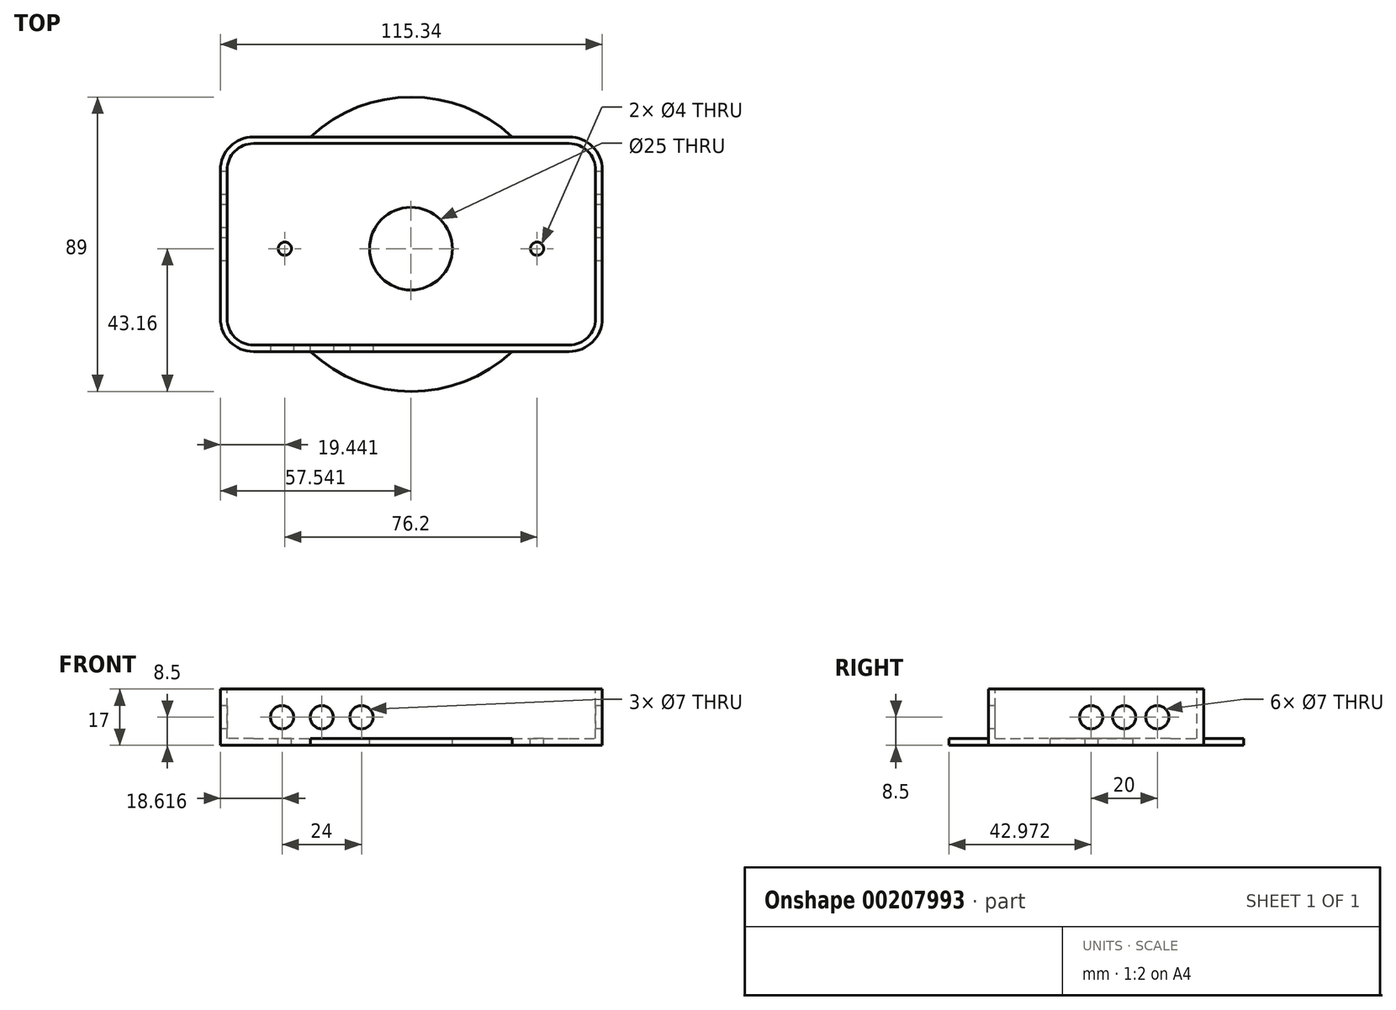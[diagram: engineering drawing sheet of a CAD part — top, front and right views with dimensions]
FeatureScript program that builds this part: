
annotation { "Feature Type Name" : "Feature", "Feature Type Description" : "" }
export const myFeature = defineFeature(function(context is Context, id is Id, definition is map)
    precondition{}
    {
        {
            var Q0;
            Q0=qCreatedBy(makeId("Top.planeOp"),FACE);
            var sketch = newSketch(context, id + "F0", { "sketchPlane" : qUnion([Q0])});
            skCircle(sketch, "E0", {"center": v(-41.46, 25.61) * mm, "radius": 3.2 * mm});
            skCircle(sketch, "E1", {"center": v(52.64, 25.61) * mm, "radius": 3.2 * mm});
            skCircle(sketch, "E2", {"center": v(52.64, -22.93) * mm, "radius": 3.2 * mm});
            skCircle(sketch, "E3", {"center": v(-41.46, -22.93) * mm, "radius": 3.2 * mm});
            skLineSegment(sketch, "E4.bottom", {"start": v(-44.66, 28.81) * mm, "end": v(55.84, 28.81) * mm});
            skLineSegment(sketch, "E4.top", {"start": v(-44.66, -26.13) * mm, "end": v(55.84, -26.13) * mm});
            skLineSegment(sketch, "E4.left", {"start": v(-44.66, 28.81) * mm, "end": v(-44.66, -26.13) * mm});
            skLineSegment(sketch, "E4.right", {"start": v(55.84, 28.81) * mm, "end": v(55.84, -26.13) * mm});
            skLineSegment(sketch, "E5.bottom", {"start": v(-29.74, 26.84) * mm, "end": v(45.76, 26.84) * mm});
            skLineSegment(sketch, "E5.top", {"start": v(-29.74, -24.16) * mm, "end": v(45.76, -24.16) * mm});
            skLineSegment(sketch, "E5.left", {"start": v(-29.74, 26.84) * mm, "end": v(-29.74, -24.16) * mm});
            skLineSegment(sketch, "E5.right", {"start": v(45.76, 26.84) * mm, "end": v(45.76, -24.16) * mm});
            skLineSegment(sketch, "E6.bottom", {"start": v(-39.66, 33.81) * mm, "end": v(55.68, 33.81) * mm});
            skLineSegment(sketch, "E6.top", {"start": v(-39.66, -31.13) * mm, "end": v(55.68, -31.13) * mm});
            skLineSegment(sketch, "E6.left", {"start": v(-49.66, 23.81) * mm, "end": v(-49.66, -21.13) * mm});
            skLineSegment(sketch, "E6.right", {"start": v(65.68, 23.81) * mm, "end": v(65.68, -21.13) * mm});
            skCircle(sketch, "E7", {"center": v(8, 1.34) * mm, "radius": 44.5 * mm});
            skPoint(sketch, "E7.centerSnap0", {"position": v(8, -24.16) * mm});
            skPoint(sketch, "E7.centerSnap1", {"position": v(-29.74, 1.34) * mm});
            skPoint(sketch, "E8.visualSharp", {"position": v(65.68, 33.81) * mm});
            skArc(sketch, "E8.filletArc", {"start": v(65.68, 23.81) * mm, "mid": v(62.75, 30.88) * mm, "end": v(55.68, 33.81) * mm});
            skPoint(sketch, "E9.visualSharp", {"position": v(-49.66, 33.81) * mm});
            skArc(sketch, "E9.filletArc", {"start": v(-39.66, 33.81) * mm, "mid": v(-46.74, 30.88) * mm, "end": v(-49.66, 23.81) * mm});
            skPoint(sketch, "E10.visualSharp", {"position": v(-49.66, -31.13) * mm});
            skArc(sketch, "E10.filletArc", {"start": v(-49.66, -21.13) * mm, "mid": v(-46.74, -28.2) * mm, "end": v(-39.66, -31.13) * mm});
            skPoint(sketch, "E11.visualSharp", {"position": v(65.68, -31.13) * mm});
            skArc(sketch, "E11.filletArc", {"start": v(55.68, -31.13) * mm, "mid": v(62.75, -28.2) * mm, "end": v(65.68, -21.13) * mm});
            skSolve(sketch);
        }
        {
            var Q0;
            {var subQ1=sQuery(id+"F0.wireOp",EDGE,"E4.bottom");var subQ13=sQuery(id+"F0.wireOp",EDGE,"E0");var subQ20=makeQuery(id+"F0.imprint","INTERSECT",VERTEX,{"disambiguationData":[OD(1.0)],"derivedFrom":[subQ13,subQ1]});Q0=makeQuery(id+"F0.imprint","IMPRINT",FACE,{"disambiguationData":[TD([[makeQuery(id+"F0.imprint","IMPRINT",EDGE,{"disambiguationData":[TD([[subQ20,1.0]])],"derivedFrom":subQ13}),-1.0]])]});}
            var Q1;
            {var subQ0=sQuery(id+"F0.wireOp",EDGE,"E7");var subQ7=sQuery(id+"F0.wireOp",EDGE,"E5.bottom");var subQ12=makeQuery(id+"F0.imprint","INTERSECT",VERTEX,{"disambiguationData":[OD(0.0)],"derivedFrom":[subQ7,subQ0]});Q1=makeQuery(id+"F0.imprint","IMPRINT",FACE,{"disambiguationData":[TD([[makeQuery(id+"F0.imprint","IMPRINT",EDGE,{"disambiguationData":[TD([[subQ12,-1.0]])],"derivedFrom":subQ7}),-1.0]])]});}
            var Q2;
            {var subQ0=sQuery(id+"F0.wireOp",EDGE,"E4.bottom");var subQ1=sQuery(id+"F0.wireOp",EDGE,"E1");var subQ2=makeQuery(id+"F0.imprint","INTERSECT",VERTEX,{"disambiguationData":[OD(0.0)],"derivedFrom":[subQ1,subQ0]});Q2=makeQuery(id+"F0.imprint","IMPRINT",FACE,{"disambiguationData":[TD([[makeQuery(id+"F0.imprint","IMPRINT",EDGE,{"disambiguationData":[TD([[subQ2,1.0]])],"derivedFrom":subQ1}),1.0]])]});}
            var Q3;
            {var subQ0=sQuery(id+"F0.wireOp",EDGE,"E4.left");var subQ1=sQuery(id+"F0.wireOp",EDGE,"E3");var subQ2=makeQuery(id+"F0.imprint","INTERSECT",VERTEX,{"disambiguationData":[OD(0.0)],"derivedFrom":[subQ1,subQ0]});Q3=makeQuery(id+"F0.imprint","IMPRINT",FACE,{"disambiguationData":[TD([[makeQuery(id+"F0.imprint","IMPRINT",EDGE,{"disambiguationData":[TD([[subQ2,-1.0]])],"derivedFrom":subQ1}),1.0]])]});}
            var Q4;
            {var subQ0=sQuery(id+"F0.wireOp",EDGE,"E7");var subQ1=sQuery(id+"F0.wireOp",EDGE,"E4.top");var subQ2=makeQuery(id+"F0.imprint","INTERSECT",VERTEX,{"disambiguationData":[OD(0.0)],"derivedFrom":[subQ1,subQ0]});Q4=makeQuery(id+"F0.imprint","IMPRINT",FACE,{"disambiguationData":[TD([[makeQuery(id+"F0.imprint","IMPRINT",EDGE,{"disambiguationData":[TD([[subQ2,-1.0]])],"derivedFrom":subQ1}),-1.0]])]});}
            var Q5;
            {var subQ0=sQuery(id+"F0.wireOp",EDGE,"E7");var subQ1=sQuery(id+"F0.wireOp",EDGE,"E4.top");var subQ2=makeQuery(id+"F0.imprint","INTERSECT",VERTEX,{"disambiguationData":[OD(0.0)],"derivedFrom":[subQ1,subQ0]});Q5=makeQuery(id+"F0.imprint","IMPRINT",FACE,{"disambiguationData":[TD([[makeQuery(id+"F0.imprint","IMPRINT",EDGE,{"disambiguationData":[TD([[subQ2,-1.0]])],"derivedFrom":subQ1}),1.0]])]});}
            var Q6;
            {var subQ0=sQuery(id+"F0.wireOp",EDGE,"E7");var subQ1=sQuery(id+"F0.wireOp",EDGE,"E6.top");var subQ2=makeQuery(id+"F0.imprint","INTERSECT",VERTEX,{"disambiguationData":[OD(0.0)],"derivedFrom":[subQ1,subQ0]});Q6=makeQuery(id+"F0.imprint","IMPRINT",FACE,{"disambiguationData":[TD([[makeQuery(id+"F0.imprint","IMPRINT",EDGE,{"disambiguationData":[TD([[subQ2,-1.0]])],"derivedFrom":subQ1}),-1.0]])]});}
            var Q7;
            {var subQ0=sQuery(id+"F0.wireOp",EDGE,"E7");var subQ1=sQuery(id+"F0.wireOp",EDGE,"E6.bottom");var subQ2=makeQuery(id+"F0.imprint","INTERSECT",VERTEX,{"disambiguationData":[OD(0.0)],"derivedFrom":[subQ1,subQ0]});Q7=makeQuery(id+"F0.imprint","IMPRINT",FACE,{"disambiguationData":[TD([[makeQuery(id+"F0.imprint","IMPRINT",EDGE,{"disambiguationData":[TD([[subQ2,-1.0]])],"derivedFrom":subQ1}),1.0]])]});}
            var Q8;
            Q8=makeQuery(id+"F0.imprint","IMPRINT",FACE,{"disambiguationData":[TD([[makeQuery(id+"F0.imprint","IMPRINT",EDGE,{"derivedFrom":sQuery(id+"F0.wireOp",EDGE,"E6.right")}),-1.0]])]});
            var Q9;
            {var subQ1=sQuery(id+"F0.wireOp",EDGE,"E4.bottom");var subQ5=sQuery(id+"F0.wireOp",EDGE,"E1");var subQ6=makeQuery(id+"F0.imprint","INTERSECT",VERTEX,{"disambiguationData":[OD(1.0)],"derivedFrom":[subQ5,subQ1]});Q9=makeQuery(id+"F0.imprint","IMPRINT",FACE,{"disambiguationData":[TD([[makeQuery(id+"F0.imprint","IMPRINT",EDGE,{"disambiguationData":[TD([[subQ6,-1.0]])],"derivedFrom":subQ5}),-1.0]])]});}
            var Q10;
            {var subQ0=sQuery(id+"F0.wireOp",EDGE,"E4.bottom");var subQ1=sQuery(id+"F0.wireOp",EDGE,"E0");var subQ2=makeQuery(id+"F0.imprint","INTERSECT",VERTEX,{"disambiguationData":[OD(0.0)],"derivedFrom":[subQ1,subQ0]});Q10=makeQuery(id+"F0.imprint","IMPRINT",FACE,{"disambiguationData":[TD([[makeQuery(id+"F0.imprint","IMPRINT",EDGE,{"disambiguationData":[TD([[subQ2,-1.0]])],"derivedFrom":subQ1}),1.0]])]});}
            var Q11;
            {var subQ0=sQuery(id+"F0.wireOp",EDGE,"E7");var subQ1=sQuery(id+"F0.wireOp",EDGE,"E4.bottom");var subQ2=makeQuery(id+"F0.imprint","INTERSECT",VERTEX,{"disambiguationData":[OD(0.0)],"derivedFrom":[subQ1,subQ0]});Q11=makeQuery(id+"F0.imprint","IMPRINT",FACE,{"disambiguationData":[TD([[makeQuery(id+"F0.imprint","IMPRINT",EDGE,{"disambiguationData":[TD([[subQ2,-1.0]])],"derivedFrom":subQ1}),-1.0]])]});}
            var Q12;
            {var subQ0=sQuery(id+"F0.wireOp",EDGE,"E7");var subQ1=sQuery(id+"F0.wireOp",EDGE,"E5.left");var subQ2=makeQuery(id+"F0.imprint","INTERSECT",VERTEX,{"disambiguationData":[OD(0.0)],"derivedFrom":[subQ1,subQ0]});Q12=makeQuery(id+"F0.imprint","IMPRINT",FACE,{"disambiguationData":[TD([[makeQuery(id+"F0.imprint","IMPRINT",EDGE,{"disambiguationData":[TD([[subQ2,-1.0]])],"derivedFrom":subQ1}),-1.0]])]});}
            var Q13;
            Q13=makeQuery(id+"F0.imprint","IMPRINT",FACE,{"disambiguationData":[TD([[makeQuery(id+"F0.imprint","IMPRINT",EDGE,{"derivedFrom":sQuery(id+"F0.wireOp",EDGE,"E6.left")}),1.0]])]});
            var Q14;
            {var subQ0=sQuery(id+"F0.wireOp",EDGE,"E4.top");var subQ1=sQuery(id+"F0.wireOp",EDGE,"E2");var subQ2=makeQuery(id+"F0.imprint","INTERSECT",VERTEX,{"disambiguationData":[OD(0.0)],"derivedFrom":[subQ1,subQ0]});Q14=makeQuery(id+"F0.imprint","IMPRINT",FACE,{"disambiguationData":[TD([[makeQuery(id+"F0.imprint","IMPRINT",EDGE,{"disambiguationData":[TD([[subQ2,1.0]])],"derivedFrom":subQ1}),1.0]])]});}
            var Q15;
            {var subQ0=sQuery(id+"F0.wireOp",EDGE,"E7");var subQ1=sQuery(id+"F0.wireOp",EDGE,"E5.right");var subQ2=makeQuery(id+"F0.imprint","INTERSECT",VERTEX,{"disambiguationData":[OD(0.0)],"derivedFrom":[subQ1,subQ0]});Q15=makeQuery(id+"F0.imprint","IMPRINT",FACE,{"disambiguationData":[TD([[makeQuery(id+"F0.imprint","IMPRINT",EDGE,{"disambiguationData":[TD([[subQ2,-1.0]])],"derivedFrom":subQ1}),1.0]])]});}
            var Q16;
            {var subQ0=sQuery(id+"F0.wireOp",EDGE,"E7");var subQ1=sQuery(id+"F0.wireOp",EDGE,"E4.bottom");var subQ2=makeQuery(id+"F0.imprint","INTERSECT",VERTEX,{"disambiguationData":[OD(0.0)],"derivedFrom":[subQ1,subQ0]});Q16=makeQuery(id+"F0.imprint","IMPRINT",FACE,{"disambiguationData":[TD([[makeQuery(id+"F0.imprint","IMPRINT",EDGE,{"disambiguationData":[TD([[subQ2,-1.0]])],"derivedFrom":subQ1}),1.0]])]});}
            var Q17;
            {var subQ0=sQuery(id+"F0.wireOp",EDGE,"E5.right");var subQ1=sQuery(id+"F0.wireOp",EDGE,"E5.top");var subQ2=makeQuery(id+"F0.imprint","INTERSECT",VERTEX,{"derivedFrom":[subQ1,subQ0]});Q17=makeQuery(id+"F0.imprint","IMPRINT",FACE,{"disambiguationData":[TD([[makeQuery(id+"F0.imprint","IMPRINT",EDGE,{"disambiguationData":[TD([[subQ2,1.0]])],"derivedFrom":subQ1}),1.0]])]});}
            var Q18;
            {var subQ0=sQuery(id+"F0.wireOp",EDGE,"E4.left");var subQ1=sQuery(id+"F0.wireOp",EDGE,"E3");var subQ2=makeQuery(id+"F0.imprint","INTERSECT",VERTEX,{"disambiguationData":[OD(0.0)],"derivedFrom":[subQ1,subQ0]});Q18=makeQuery(id+"F0.imprint","IMPRINT",FACE,{"disambiguationData":[TD([[makeQuery(id+"F0.imprint","IMPRINT",EDGE,{"disambiguationData":[TD([[subQ2,1.0]])],"derivedFrom":subQ1}),1.0]])]});}
            var Q19;
            {var subQ0=sQuery(id+"F0.wireOp",EDGE,"E4.left");var subQ1=sQuery(id+"F0.wireOp",EDGE,"E3");var subQ2=makeQuery(id+"F0.imprint","INTERSECT",VERTEX,{"disambiguationData":[OD(0.0)],"derivedFrom":[subQ1,subQ0]});Q19=makeQuery(id+"F0.imprint","IMPRINT",FACE,{"disambiguationData":[TD([[makeQuery(id+"F0.imprint","IMPRINT",EDGE,{"disambiguationData":[TD([[subQ2,-1.0]])],"derivedFrom":subQ1}),-1.0]])]});}
            var Q20;
            {var subQ0=sQuery(id+"F0.wireOp",EDGE,"E4.right");var subQ1=sQuery(id+"F0.wireOp",EDGE,"E2");var subQ2=makeQuery(id+"F0.imprint","INTERSECT",VERTEX,{"disambiguationData":[OD(0.0)],"derivedFrom":[subQ1,subQ0]});Q20=makeQuery(id+"F0.imprint","IMPRINT",FACE,{"disambiguationData":[TD([[makeQuery(id+"F0.imprint","IMPRINT",EDGE,{"disambiguationData":[TD([[subQ2,1.0]])],"derivedFrom":subQ1}),1.0]])]});}
            var Q21;
            {var subQ0=sQuery(id+"F0.wireOp",EDGE,"E4.top");var subQ1=sQuery(id+"F0.wireOp",EDGE,"E2");var subQ2=makeQuery(id+"F0.imprint","INTERSECT",VERTEX,{"disambiguationData":[OD(1.0)],"derivedFrom":[subQ1,subQ0]});Q21=makeQuery(id+"F0.imprint","IMPRINT",FACE,{"disambiguationData":[TD([[makeQuery(id+"F0.imprint","IMPRINT",EDGE,{"disambiguationData":[TD([[subQ2,-1.0]])],"derivedFrom":subQ1}),-1.0]])]});}
            var Q22;
            {var subQ0=sQuery(id+"F0.wireOp",EDGE,"E4.top");var subQ1=sQuery(id+"F0.wireOp",EDGE,"E2");var subQ2=makeQuery(id+"F0.imprint","INTERSECT",VERTEX,{"disambiguationData":[OD(0.0)],"derivedFrom":[subQ1,subQ0]});Q22=makeQuery(id+"F0.imprint","IMPRINT",FACE,{"disambiguationData":[TD([[makeQuery(id+"F0.imprint","IMPRINT",EDGE,{"disambiguationData":[TD([[subQ2,-1.0]])],"derivedFrom":subQ1}),1.0]])]});}
            var Q23;
            {var subQ0=sQuery(id+"F0.wireOp",EDGE,"E4.bottom");var subQ1=sQuery(id+"F0.wireOp",EDGE,"E1");var subQ2=makeQuery(id+"F0.imprint","INTERSECT",VERTEX,{"disambiguationData":[OD(0.0)],"derivedFrom":[subQ1,subQ0]});Q23=makeQuery(id+"F0.imprint","IMPRINT",FACE,{"disambiguationData":[TD([[makeQuery(id+"F0.imprint","IMPRINT",EDGE,{"disambiguationData":[TD([[subQ2,-1.0]])],"derivedFrom":subQ1}),1.0]])]});}
            var Q24;
            {var subQ0=sQuery(id+"F0.wireOp",EDGE,"E4.right");var subQ1=sQuery(id+"F0.wireOp",EDGE,"E1");var subQ2=makeQuery(id+"F0.imprint","INTERSECT",VERTEX,{"disambiguationData":[OD(0.0)],"derivedFrom":[subQ1,subQ0]});Q24=makeQuery(id+"F0.imprint","IMPRINT",FACE,{"disambiguationData":[TD([[makeQuery(id+"F0.imprint","IMPRINT",EDGE,{"disambiguationData":[TD([[subQ2,1.0]])],"derivedFrom":subQ1}),1.0]])]});}
            var Q25;
            {var subQ0=sQuery(id+"F0.wireOp",EDGE,"E4.bottom");var subQ1=sQuery(id+"F0.wireOp",EDGE,"E1");var subQ2=makeQuery(id+"F0.imprint","INTERSECT",VERTEX,{"disambiguationData":[OD(0.0)],"derivedFrom":[subQ1,subQ0]});Q25=makeQuery(id+"F0.imprint","IMPRINT",FACE,{"disambiguationData":[TD([[makeQuery(id+"F0.imprint","IMPRINT",EDGE,{"disambiguationData":[TD([[subQ2,1.0]])],"derivedFrom":subQ1}),-1.0]])]});}
            var Q26;
            {var subQ0=sQuery(id+"F0.wireOp",EDGE,"E4.left");var subQ1=sQuery(id+"F0.wireOp",EDGE,"E0");var subQ2=makeQuery(id+"F0.imprint","INTERSECT",VERTEX,{"disambiguationData":[OD(0.0)],"derivedFrom":[subQ1,subQ0]});Q26=makeQuery(id+"F0.imprint","IMPRINT",FACE,{"disambiguationData":[TD([[makeQuery(id+"F0.imprint","IMPRINT",EDGE,{"disambiguationData":[TD([[subQ2,-1.0]])],"derivedFrom":subQ1}),1.0]])]});}
            var Q27;
            {var subQ0=sQuery(id+"F0.wireOp",EDGE,"E4.bottom");var subQ1=sQuery(id+"F0.wireOp",EDGE,"E0");var subQ2=makeQuery(id+"F0.imprint","INTERSECT",VERTEX,{"disambiguationData":[OD(0.0)],"derivedFrom":[subQ1,subQ0]});Q27=makeQuery(id+"F0.imprint","IMPRINT",FACE,{"disambiguationData":[TD([[makeQuery(id+"F0.imprint","IMPRINT",EDGE,{"disambiguationData":[TD([[subQ2,-1.0]])],"derivedFrom":subQ1}),-1.0]])]});}
            var Q28;
            {var subQ0=sQuery(id+"F0.wireOp",EDGE,"E4.bottom");var subQ1=sQuery(id+"F0.wireOp",EDGE,"E0");var subQ2=makeQuery(id+"F0.imprint","INTERSECT",VERTEX,{"disambiguationData":[OD(0.0)],"derivedFrom":[subQ1,subQ0]});Q28=makeQuery(id+"F0.imprint","IMPRINT",FACE,{"disambiguationData":[TD([[makeQuery(id+"F0.imprint","IMPRINT",EDGE,{"disambiguationData":[TD([[subQ2,1.0]])],"derivedFrom":subQ1}),1.0]])]});}
            var Q29;
            {var subQ0=sQuery(id+"F0.wireOp",EDGE,"E5.left");var subQ1=sQuery(id+"F0.wireOp",EDGE,"E5.top");var subQ2=makeQuery(id+"F0.imprint","INTERSECT",VERTEX,{"derivedFrom":[subQ1,subQ0]});Q29=makeQuery(id+"F0.imprint","IMPRINT",FACE,{"disambiguationData":[TD([[makeQuery(id+"F0.imprint","IMPRINT",EDGE,{"disambiguationData":[TD([[subQ2,-1.0]])],"derivedFrom":subQ1}),1.0]])]});}
            var Q30;
            {var subQ0=sQuery(id+"F0.wireOp",EDGE,"E5.left");var subQ1=sQuery(id+"F0.wireOp",EDGE,"E5.bottom");var subQ2=makeQuery(id+"F0.imprint","INTERSECT",VERTEX,{"derivedFrom":[subQ1,subQ0]});Q30=makeQuery(id+"F0.imprint","IMPRINT",FACE,{"disambiguationData":[TD([[makeQuery(id+"F0.imprint","IMPRINT",EDGE,{"disambiguationData":[TD([[subQ2,-1.0]])],"derivedFrom":subQ1}),-1.0]])]});}
            var Q31;
            {var subQ0=sQuery(id+"F0.wireOp",EDGE,"E4.top");var subQ1=sQuery(id+"F0.wireOp",EDGE,"E3");var subQ2=makeQuery(id+"F0.imprint","INTERSECT",VERTEX,{"disambiguationData":[OD(0.0)],"derivedFrom":[subQ1,subQ0]});Q31=makeQuery(id+"F0.imprint","IMPRINT",FACE,{"disambiguationData":[TD([[makeQuery(id+"F0.imprint","IMPRINT",EDGE,{"disambiguationData":[TD([[subQ2,-1.0]])],"derivedFrom":subQ1}),1.0]])]});}
            var Q32;
            {var subQ0=sQuery(id+"F0.wireOp",EDGE,"E5.right");var subQ1=sQuery(id+"F0.wireOp",EDGE,"E5.bottom");var subQ2=makeQuery(id+"F0.imprint","INTERSECT",VERTEX,{"derivedFrom":[subQ1,subQ0]});Q32=makeQuery(id+"F0.imprint","IMPRINT",FACE,{"disambiguationData":[TD([[makeQuery(id+"F0.imprint","IMPRINT",EDGE,{"disambiguationData":[TD([[subQ2,1.0]])],"derivedFrom":subQ1}),-1.0]])]});}
            extrude(context, id + "F1", {"entities" : qUnion([Q0, Q1, Q2, Q3, Q4, Q5, Q6, Q7, Q8, Q9, Q10, Q11, Q12, Q13, Q14, Q15, Q16, Q17, Q18, Q19, Q20, Q21, Q22, Q23, Q24, Q25, Q26, Q27, Q28, Q29, Q30, Q31, Q32]), "oppositeDirection" : true, "depth" : 2 * mm});
        }
        {
            var Q0;
            Q0=makeQuery(id+"F0.imprint","IMPRINT",FACE,{"disambiguationData":[TD([[makeQuery(id+"F0.imprint","IMPRINT",EDGE,{"derivedFrom":sQuery(id+"F0.wireOp",EDGE,"E6.left")}),1.0]])]});
            var Q1;
            {var subQ0=sQuery(id+"F0.wireOp",EDGE,"E7");var subQ1=sQuery(id+"F0.wireOp",EDGE,"E4.bottom");var subQ2=makeQuery(id+"F0.imprint","INTERSECT",VERTEX,{"disambiguationData":[OD(0.0)],"derivedFrom":[subQ1,subQ0]});Q1=makeQuery(id+"F0.imprint","IMPRINT",FACE,{"disambiguationData":[TD([[makeQuery(id+"F0.imprint","IMPRINT",EDGE,{"disambiguationData":[TD([[subQ2,-1.0]])],"derivedFrom":subQ1}),1.0]])]});}
            var Q2;
            Q2=makeQuery(id+"F0.imprint","IMPRINT",FACE,{"disambiguationData":[TD([[makeQuery(id+"F0.imprint","IMPRINT",EDGE,{"derivedFrom":sQuery(id+"F0.wireOp",EDGE,"E6.right")}),-1.0]])]});
            var Q3;
            {var subQ1=sQuery(id+"F0.wireOp",EDGE,"E4.bottom");var subQ5=sQuery(id+"F0.wireOp",EDGE,"E1");var subQ6=makeQuery(id+"F0.imprint","INTERSECT",VERTEX,{"disambiguationData":[OD(1.0)],"derivedFrom":[subQ5,subQ1]});Q3=makeQuery(id+"F0.imprint","IMPRINT",FACE,{"disambiguationData":[TD([[makeQuery(id+"F0.imprint","IMPRINT",EDGE,{"disambiguationData":[TD([[subQ6,-1.0]])],"derivedFrom":subQ5}),-1.0]])]});}
            var Q4;
            {var subQ0=sQuery(id+"F0.wireOp",EDGE,"E4.bottom");var subQ1=sQuery(id+"F0.wireOp",EDGE,"E1");var subQ2=makeQuery(id+"F0.imprint","INTERSECT",VERTEX,{"disambiguationData":[OD(0.0)],"derivedFrom":[subQ1,subQ0]});Q4=makeQuery(id+"F0.imprint","IMPRINT",FACE,{"disambiguationData":[TD([[makeQuery(id+"F0.imprint","IMPRINT",EDGE,{"disambiguationData":[TD([[subQ2,1.0]])],"derivedFrom":subQ1}),1.0]])]});}
            var Q5;
            {var subQ0=sQuery(id+"F0.wireOp",EDGE,"E4.top");var subQ1=sQuery(id+"F0.wireOp",EDGE,"E2");var subQ2=makeQuery(id+"F0.imprint","INTERSECT",VERTEX,{"disambiguationData":[OD(0.0)],"derivedFrom":[subQ1,subQ0]});Q5=makeQuery(id+"F0.imprint","IMPRINT",FACE,{"disambiguationData":[TD([[makeQuery(id+"F0.imprint","IMPRINT",EDGE,{"disambiguationData":[TD([[subQ2,1.0]])],"derivedFrom":subQ1}),1.0]])]});}
            var Q6;
            {var subQ0=sQuery(id+"F0.wireOp",EDGE,"E7");var subQ1=sQuery(id+"F0.wireOp",EDGE,"E5.right");var subQ2=makeQuery(id+"F0.imprint","INTERSECT",VERTEX,{"disambiguationData":[OD(0.0)],"derivedFrom":[subQ1,subQ0]});Q6=makeQuery(id+"F0.imprint","IMPRINT",FACE,{"disambiguationData":[TD([[makeQuery(id+"F0.imprint","IMPRINT",EDGE,{"disambiguationData":[TD([[subQ2,-1.0]])],"derivedFrom":subQ1}),1.0]])]});}
            var Q7;
            {var subQ0=sQuery(id+"F0.wireOp",EDGE,"E7");var subQ7=sQuery(id+"F0.wireOp",EDGE,"E5.bottom");var subQ12=makeQuery(id+"F0.imprint","INTERSECT",VERTEX,{"disambiguationData":[OD(0.0)],"derivedFrom":[subQ7,subQ0]});Q7=makeQuery(id+"F0.imprint","IMPRINT",FACE,{"disambiguationData":[TD([[makeQuery(id+"F0.imprint","IMPRINT",EDGE,{"disambiguationData":[TD([[subQ12,-1.0]])],"derivedFrom":subQ7}),-1.0]])]});}
            var Q8;
            {var subQ0=sQuery(id+"F0.wireOp",EDGE,"E7");var subQ1=sQuery(id+"F0.wireOp",EDGE,"E4.bottom");var subQ2=makeQuery(id+"F0.imprint","INTERSECT",VERTEX,{"disambiguationData":[OD(0.0)],"derivedFrom":[subQ1,subQ0]});Q8=makeQuery(id+"F0.imprint","IMPRINT",FACE,{"disambiguationData":[TD([[makeQuery(id+"F0.imprint","IMPRINT",EDGE,{"disambiguationData":[TD([[subQ2,-1.0]])],"derivedFrom":subQ1}),-1.0]])]});}
            var Q9;
            {var subQ0=sQuery(id+"F0.wireOp",EDGE,"E7");var subQ1=sQuery(id+"F0.wireOp",EDGE,"E4.top");var subQ2=makeQuery(id+"F0.imprint","INTERSECT",VERTEX,{"disambiguationData":[OD(0.0)],"derivedFrom":[subQ1,subQ0]});Q9=makeQuery(id+"F0.imprint","IMPRINT",FACE,{"disambiguationData":[TD([[makeQuery(id+"F0.imprint","IMPRINT",EDGE,{"disambiguationData":[TD([[subQ2,-1.0]])],"derivedFrom":subQ1}),-1.0]])]});}
            var Q10;
            {var subQ0=sQuery(id+"F0.wireOp",EDGE,"E7");var subQ1=sQuery(id+"F0.wireOp",EDGE,"E4.top");var subQ2=makeQuery(id+"F0.imprint","INTERSECT",VERTEX,{"disambiguationData":[OD(0.0)],"derivedFrom":[subQ1,subQ0]});Q10=makeQuery(id+"F0.imprint","IMPRINT",FACE,{"disambiguationData":[TD([[makeQuery(id+"F0.imprint","IMPRINT",EDGE,{"disambiguationData":[TD([[subQ2,-1.0]])],"derivedFrom":subQ1}),1.0]])]});}
            var Q11;
            {var subQ0=sQuery(id+"F0.wireOp",EDGE,"E7");var subQ1=sQuery(id+"F0.wireOp",EDGE,"E5.left");var subQ2=makeQuery(id+"F0.imprint","INTERSECT",VERTEX,{"disambiguationData":[OD(0.0)],"derivedFrom":[subQ1,subQ0]});Q11=makeQuery(id+"F0.imprint","IMPRINT",FACE,{"disambiguationData":[TD([[makeQuery(id+"F0.imprint","IMPRINT",EDGE,{"disambiguationData":[TD([[subQ2,-1.0]])],"derivedFrom":subQ1}),-1.0]])]});}
            var Q12;
            {var subQ1=sQuery(id+"F0.wireOp",EDGE,"E4.bottom");var subQ13=sQuery(id+"F0.wireOp",EDGE,"E0");var subQ20=makeQuery(id+"F0.imprint","INTERSECT",VERTEX,{"disambiguationData":[OD(1.0)],"derivedFrom":[subQ13,subQ1]});Q12=makeQuery(id+"F0.imprint","IMPRINT",FACE,{"disambiguationData":[TD([[makeQuery(id+"F0.imprint","IMPRINT",EDGE,{"disambiguationData":[TD([[subQ20,1.0]])],"derivedFrom":subQ13}),-1.0]])]});}
            var Q13;
            {var subQ0=sQuery(id+"F0.wireOp",EDGE,"E4.left");var subQ1=sQuery(id+"F0.wireOp",EDGE,"E3");var subQ2=makeQuery(id+"F0.imprint","INTERSECT",VERTEX,{"disambiguationData":[OD(0.0)],"derivedFrom":[subQ1,subQ0]});Q13=makeQuery(id+"F0.imprint","IMPRINT",FACE,{"disambiguationData":[TD([[makeQuery(id+"F0.imprint","IMPRINT",EDGE,{"disambiguationData":[TD([[subQ2,-1.0]])],"derivedFrom":subQ1}),1.0]])]});}
            var Q14;
            {var subQ0=sQuery(id+"F0.wireOp",EDGE,"E4.bottom");var subQ1=sQuery(id+"F0.wireOp",EDGE,"E0");var subQ2=makeQuery(id+"F0.imprint","INTERSECT",VERTEX,{"disambiguationData":[OD(0.0)],"derivedFrom":[subQ1,subQ0]});Q14=makeQuery(id+"F0.imprint","IMPRINT",FACE,{"disambiguationData":[TD([[makeQuery(id+"F0.imprint","IMPRINT",EDGE,{"disambiguationData":[TD([[subQ2,-1.0]])],"derivedFrom":subQ1}),1.0]])]});}
            var Q15;
            {var subQ0=sQuery(id+"F0.wireOp",EDGE,"E4.bottom");var subQ1=sQuery(id+"F0.wireOp",EDGE,"E0");var subQ2=makeQuery(id+"F0.imprint","INTERSECT",VERTEX,{"disambiguationData":[OD(0.0)],"derivedFrom":[subQ1,subQ0]});Q15=makeQuery(id+"F0.imprint","IMPRINT",FACE,{"disambiguationData":[TD([[makeQuery(id+"F0.imprint","IMPRINT",EDGE,{"disambiguationData":[TD([[subQ2,-1.0]])],"derivedFrom":subQ1}),-1.0]])]});}
            var Q16;
            {var subQ0=sQuery(id+"F0.wireOp",EDGE,"E5.left");var subQ1=sQuery(id+"F0.wireOp",EDGE,"E5.bottom");var subQ2=makeQuery(id+"F0.imprint","INTERSECT",VERTEX,{"derivedFrom":[subQ1,subQ0]});Q16=makeQuery(id+"F0.imprint","IMPRINT",FACE,{"disambiguationData":[TD([[makeQuery(id+"F0.imprint","IMPRINT",EDGE,{"disambiguationData":[TD([[subQ2,-1.0]])],"derivedFrom":subQ1}),-1.0]])]});}
            var Q17;
            {var subQ0=sQuery(id+"F0.wireOp",EDGE,"E4.left");var subQ1=sQuery(id+"F0.wireOp",EDGE,"E3");var subQ2=makeQuery(id+"F0.imprint","INTERSECT",VERTEX,{"disambiguationData":[OD(0.0)],"derivedFrom":[subQ1,subQ0]});Q17=makeQuery(id+"F0.imprint","IMPRINT",FACE,{"disambiguationData":[TD([[makeQuery(id+"F0.imprint","IMPRINT",EDGE,{"disambiguationData":[TD([[subQ2,-1.0]])],"derivedFrom":subQ1}),-1.0]])]});}
            var Q18;
            {var subQ0=sQuery(id+"F0.wireOp",EDGE,"E5.left");var subQ1=sQuery(id+"F0.wireOp",EDGE,"E5.top");var subQ2=makeQuery(id+"F0.imprint","INTERSECT",VERTEX,{"derivedFrom":[subQ1,subQ0]});Q18=makeQuery(id+"F0.imprint","IMPRINT",FACE,{"disambiguationData":[TD([[makeQuery(id+"F0.imprint","IMPRINT",EDGE,{"disambiguationData":[TD([[subQ2,-1.0]])],"derivedFrom":subQ1}),1.0]])]});}
            var Q19;
            {var subQ0=sQuery(id+"F0.wireOp",EDGE,"E5.right");var subQ1=sQuery(id+"F0.wireOp",EDGE,"E5.bottom");var subQ2=makeQuery(id+"F0.imprint","INTERSECT",VERTEX,{"derivedFrom":[subQ1,subQ0]});Q19=makeQuery(id+"F0.imprint","IMPRINT",FACE,{"disambiguationData":[TD([[makeQuery(id+"F0.imprint","IMPRINT",EDGE,{"disambiguationData":[TD([[subQ2,1.0]])],"derivedFrom":subQ1}),-1.0]])]});}
            var Q20;
            {var subQ0=sQuery(id+"F0.wireOp",EDGE,"E4.bottom");var subQ1=sQuery(id+"F0.wireOp",EDGE,"E1");var subQ2=makeQuery(id+"F0.imprint","INTERSECT",VERTEX,{"disambiguationData":[OD(0.0)],"derivedFrom":[subQ1,subQ0]});Q20=makeQuery(id+"F0.imprint","IMPRINT",FACE,{"disambiguationData":[TD([[makeQuery(id+"F0.imprint","IMPRINT",EDGE,{"disambiguationData":[TD([[subQ2,1.0]])],"derivedFrom":subQ1}),-1.0]])]});}
            var Q21;
            {var subQ0=sQuery(id+"F0.wireOp",EDGE,"E5.right");var subQ1=sQuery(id+"F0.wireOp",EDGE,"E5.top");var subQ2=makeQuery(id+"F0.imprint","INTERSECT",VERTEX,{"derivedFrom":[subQ1,subQ0]});Q21=makeQuery(id+"F0.imprint","IMPRINT",FACE,{"disambiguationData":[TD([[makeQuery(id+"F0.imprint","IMPRINT",EDGE,{"disambiguationData":[TD([[subQ2,1.0]])],"derivedFrom":subQ1}),1.0]])]});}
            var Q22;
            {var subQ0=sQuery(id+"F0.wireOp",EDGE,"E4.top");var subQ1=sQuery(id+"F0.wireOp",EDGE,"E2");var subQ2=makeQuery(id+"F0.imprint","INTERSECT",VERTEX,{"disambiguationData":[OD(1.0)],"derivedFrom":[subQ1,subQ0]});Q22=makeQuery(id+"F0.imprint","IMPRINT",FACE,{"disambiguationData":[TD([[makeQuery(id+"F0.imprint","IMPRINT",EDGE,{"disambiguationData":[TD([[subQ2,-1.0]])],"derivedFrom":subQ1}),-1.0]])]});}
            extrude(context, id + "F2", {"entities" : qUnion([Q0, Q1, Q2, Q3, Q4, Q5, Q6, Q7, Q8, Q9, Q10, Q11, Q12, Q13, Q14, Q15, Q16, Q17, Q18, Q19, Q20, Q21, Q22]), "operationType" : NewBodyOperationType.ADD, "depth" : 15 * mm});
        }
        {
            var Q0;
            Q0=makeQuery(id+"F2.opExtrude","CAP_FACE",FACE,{"disambiguationData":[OSD([sQuery(id+"F0.wireOp",EDGE,"E6.bottom"),sQuery(id+"F0.wireOp",EDGE,"E6.top"),sQuery(id+"F0.wireOp",EDGE,"E6.left"),sQuery(id+"F0.wireOp",EDGE,"E6.right"),sQuery(id+"F0.wireOp",EDGE,"E8.filletArc"),sQuery(id+"F0.wireOp",EDGE,"E9.filletArc"),sQuery(id+"F0.wireOp",EDGE,"E10.filletArc"),sQuery(id+"F0.wireOp",EDGE,"E11.filletArc")])],"isStart":false});
            shell(context, id + "F3", {"entities" : qUnion([Q0]), "thickness" : 2 * mm});
        }
        {
            var Q0;
            {var subQ0=sQuery(id+"F0.wireOp",EDGE,"E7");var subQ7=sQuery(id+"F0.wireOp",EDGE,"E5.bottom");var subQ12=makeQuery(id+"F0.imprint","INTERSECT",VERTEX,{"disambiguationData":[OD(0.0)],"derivedFrom":[subQ7,subQ0]});Q0=makeQuery(id+"F0.imprint","IMPRINT",FACE,{"disambiguationData":[TD([[makeQuery(id+"F0.imprint","IMPRINT",EDGE,{"disambiguationData":[TD([[subQ12,-1.0]])],"derivedFrom":subQ7}),-1.0]])]});}
            var sketch = newSketch(context, id + "F4", { "sketchPlane" : qUnion([Q0])});
            skCircle(sketch, "E12", {"center": v(7.88, 0) * mm, "radius": 12.5 * mm});
            skCircle(sketch, "E13", {"center": v(7.88, 0) * mm, "radius": 38.1 * mm, "construction": true});
            skCircle(sketch, "E14", {"center": v(45.98, 0) * mm, "radius": 2 * mm});
            skCircle(sketch, "E15", {"center": v(-30.22, 0) * mm, "radius": 2 * mm});
            skSolve(sketch);
        }
        {
            var Q0;
            {var subQ0=sQuery(id+"F4.wireOp",EDGE,"E14");var subQ1=sQuery(id+"F0.wireOp",EDGE,"E7");var subQ2=sQuery(id+"F0.wireOp",EDGE,"E5.right");var subQ3=makeQuery(id+"F0.imprint","IMPRINT",EDGE,{"disambiguationData":[TD([[makeQuery(id+"F0.imprint","INTERSECT",VERTEX,{"disambiguationData":[OD(0.0)],"derivedFrom":[subQ2,subQ1]}),-1.0]])],"derivedFrom":subQ2});var subQ4=makeQuery(id+"F4.imprint","INTERSECT",VERTEX,{"disambiguationData":[OD(0.0)],"derivedFrom":[subQ3,subQ0]});Q0=makeQuery(id+"F4.imprint","IMPRINT",FACE,{"disambiguationData":[TD([[makeQuery(id+"F4.imprint","IMPRINT",EDGE,{"disambiguationData":[TD([[subQ4,1.0]])],"derivedFrom":subQ0}),1.0]])]});}
            var Q1;
            {var subQ0=sQuery(id+"F4.wireOp",EDGE,"E14");var subQ1=sQuery(id+"F0.wireOp",EDGE,"E7");var subQ2=sQuery(id+"F0.wireOp",EDGE,"E5.right");var subQ3=makeQuery(id+"F0.imprint","IMPRINT",EDGE,{"disambiguationData":[TD([[makeQuery(id+"F0.imprint","INTERSECT",VERTEX,{"disambiguationData":[OD(0.0)],"derivedFrom":[subQ2,subQ1]}),-1.0]])],"derivedFrom":subQ2});var subQ4=makeQuery(id+"F4.imprint","INTERSECT",VERTEX,{"disambiguationData":[OD(0.0)],"derivedFrom":[subQ3,subQ0]});Q1=makeQuery(id+"F4.imprint","IMPRINT",FACE,{"disambiguationData":[TD([[makeQuery(id+"F4.imprint","IMPRINT",EDGE,{"disambiguationData":[TD([[subQ4,-1.0]])],"derivedFrom":subQ0}),1.0]])]});}
            var Q2;
            Q2=makeQuery(id+"F4.imprint","IMPRINT",FACE,{"disambiguationData":[TD([[makeQuery(id+"F4.imprint","IMPRINT",EDGE,{"derivedFrom":sQuery(id+"F4.wireOp",EDGE,"E12")}),1.0]])]});
            var Q3;
            {var subQ0=sQuery(id+"F4.wireOp",EDGE,"E15");var subQ1=sQuery(id+"F0.wireOp",EDGE,"E7");var subQ2=sQuery(id+"F0.wireOp",EDGE,"E5.left");var subQ3=makeQuery(id+"F0.imprint","IMPRINT",EDGE,{"disambiguationData":[TD([[makeQuery(id+"F0.imprint","INTERSECT",VERTEX,{"disambiguationData":[OD(0.0)],"derivedFrom":[subQ2,subQ1]}),-1.0]])],"derivedFrom":subQ2});var subQ4=makeQuery(id+"F4.imprint","INTERSECT",VERTEX,{"disambiguationData":[OD(0.0)],"derivedFrom":[subQ3,subQ0]});Q3=makeQuery(id+"F4.imprint","IMPRINT",FACE,{"disambiguationData":[TD([[makeQuery(id+"F4.imprint","IMPRINT",EDGE,{"disambiguationData":[TD([[subQ4,1.0]])],"derivedFrom":subQ0}),1.0]])]});}
            var Q4;
            {var subQ0=sQuery(id+"F4.wireOp",EDGE,"E15");var subQ1=sQuery(id+"F0.wireOp",EDGE,"E7");var subQ2=sQuery(id+"F0.wireOp",EDGE,"E5.left");var subQ3=makeQuery(id+"F0.imprint","IMPRINT",EDGE,{"disambiguationData":[TD([[makeQuery(id+"F0.imprint","INTERSECT",VERTEX,{"disambiguationData":[OD(0.0)],"derivedFrom":[subQ2,subQ1]}),-1.0]])],"derivedFrom":subQ2});var subQ4=makeQuery(id+"F4.imprint","INTERSECT",VERTEX,{"disambiguationData":[OD(0.0)],"derivedFrom":[subQ3,subQ0]});Q4=makeQuery(id+"F4.imprint","IMPRINT",FACE,{"disambiguationData":[TD([[makeQuery(id+"F4.imprint","IMPRINT",EDGE,{"disambiguationData":[TD([[subQ4,-1.0]])],"derivedFrom":subQ0}),1.0]])]});}
            extrude(context, id + "F5", {"entities" : qUnion([Q0, Q1, Q2, Q3, Q4]), "operationType" : NewBodyOperationType.REMOVE, "endBound" : BoundingType.THROUGH_ALL, "oppositeDirection" : true, "depth" : 25 * mm});
        }
        {
            var Q0;
            {var subQ0=sQuery(id+"F0.wireOp",EDGE,"E6.top");Q0=makeQuery(id+"F2.boolean.opBoolean","MERGE",FACE,{"derivedFrom":[makeQuery(id+"F1.opExtrude","SWEPT_FACE",FACE,{"disambiguationData":[OSD([subQ0]),TDD([makeQuery(id+"F0.imprint","IMPRINT",EDGE,{"disambiguationData":[TD([[makeQuery(id+"F0.imprint","INTERSECT",VERTEX,{"derivedFrom":[subQ0,sQuery(id+"F0.wireOp",EDGE,"E10.filletArc")]}),-1.0]])],"derivedFrom":subQ0})])]}),makeQuery(id+"F1.opExtrude","SWEPT_FACE",FACE,{"disambiguationData":[OSD([subQ0]),TDD([makeQuery(id+"F0.imprint","IMPRINT",EDGE,{"disambiguationData":[TD([[makeQuery(id+"F0.imprint","INTERSECT",VERTEX,{"derivedFrom":[subQ0,sQuery(id+"F0.wireOp",EDGE,"E11.filletArc")]}),1.0]])],"derivedFrom":subQ0})])]}),makeQuery(id+"F2.opExtrude","SWEPT_FACE",FACE,{"disambiguationData":[OSD([subQ0])]})]});}
            var sketch = newSketch(context, id + "F6", { "sketchPlane" : qUnion([Q0])});
            skCircle(sketch, "E16", {"center": v(-31.04, 6.5) * mm, "radius": 3.5 * mm});
            skPoint(sketch, "E16.centerSnap0", {"position": v(-31.04, -2) * mm});
            skPoint(sketch, "E16.centerSnap1", {"position": v(-39.66, 6.5) * mm});
            skCircle(sketch, "E17.1.0.0", {"center": v(-19.04, 6.5) * mm, "radius": 3.5 * mm});
            skCircle(sketch, "E17.2.0.0", {"center": v(-7.04, 6.5) * mm, "radius": 3.5 * mm});
            skLineSegment(sketch, "E17.direction1", {"start": v(-31.04, 6.5) * mm, "end": v(-19.04, 6.5) * mm, "construction": true});
            skSolve(sketch);
        }
        {
            var Q0;
            Q0=makeQuery(id+"F6.imprint","IMPRINT",FACE,{"disambiguationData":[TD([[makeQuery(id+"F6.imprint","IMPRINT",EDGE,{"derivedFrom":sQuery(id+"F6.wireOp",EDGE,"E16")}),1.0]])]});
            var Q1;
            Q1=makeQuery(id+"F6.imprint","IMPRINT",FACE,{"disambiguationData":[TD([[makeQuery(id+"F6.imprint","IMPRINT",EDGE,{"derivedFrom":sQuery(id+"F6.wireOp",EDGE,"E17.1.0.0")}),1.0]])]});
            var Q2;
            Q2=makeQuery(id+"F6.imprint","IMPRINT",FACE,{"disambiguationData":[TD([[makeQuery(id+"F6.imprint","IMPRINT",EDGE,{"derivedFrom":sQuery(id+"F6.wireOp",EDGE,"E17.2.0.0")}),1.0]])]});
            extrude(context, id + "F7", {"entities" : qUnion([Q0, Q1, Q2]), "operationType" : NewBodyOperationType.REMOVE, "oppositeDirection" : true, "depth" : 5 * mm, "offsetDistance" : 25 * mm});
        }
        {
            var Q0;
            {var subQ0=sQuery(id+"F0.wireOp",EDGE,"E6.left");Q0=makeQuery(id+"F2.boolean.opBoolean","MERGE",FACE,{"derivedFrom":[makeQuery(id+"F1.opExtrude","SWEPT_FACE",FACE,{"disambiguationData":[OSD([subQ0])]}),makeQuery(id+"F2.opExtrude","SWEPT_FACE",FACE,{"disambiguationData":[OSD([subQ0])]})]});}
            var sketch = newSketch(context, id + "F8", { "sketchPlane" : qUnion([Q0])});
            skCircle(sketch, "E18", {"center": v(-19.81, 6.5) * mm, "radius": 3.5 * mm});
            skPoint(sketch, "E18.centerSnap0", {"position": v(-23.81, 6.5) * mm});
            skCircle(sketch, "E19.1.0.0", {"center": v(-9.81, 6.5) * mm, "radius": 3.5 * mm});
            skCircle(sketch, "E19.2.0.0", {"center": v(0.19, 6.5) * mm, "radius": 3.5 * mm});
            skLineSegment(sketch, "E19.direction1", {"start": v(-19.81, 6.5) * mm, "end": v(-9.81, 6.5) * mm, "construction": true});
            skSolve(sketch);
        }
        {
            var Q0;
            Q0=makeQuery(id+"F8.imprint","IMPRINT",FACE,{"disambiguationData":[TD([[makeQuery(id+"F8.imprint","IMPRINT",EDGE,{"derivedFrom":sQuery(id+"F8.wireOp",EDGE,"E18")}),1.0]])]});
            var Q1;
            Q1=makeQuery(id+"F8.imprint","IMPRINT",FACE,{"disambiguationData":[TD([[makeQuery(id+"F8.imprint","IMPRINT",EDGE,{"derivedFrom":sQuery(id+"F8.wireOp",EDGE,"E19.1.0.0")}),1.0]])]});
            var Q2;
            Q2=makeQuery(id+"F8.imprint","IMPRINT",FACE,{"disambiguationData":[TD([[makeQuery(id+"F8.imprint","IMPRINT",EDGE,{"derivedFrom":sQuery(id+"F8.wireOp",EDGE,"E19.2.0.0")}),1.0]])]});
            extrude(context, id + "F9", {"entities" : qUnion([Q0, Q1, Q2]), "operationType" : NewBodyOperationType.REMOVE, "endBound" : BoundingType.THROUGH_ALL, "oppositeDirection" : true, "depth" : 25 * mm, "offsetDistance" : 25 * mm});
        }
    });
